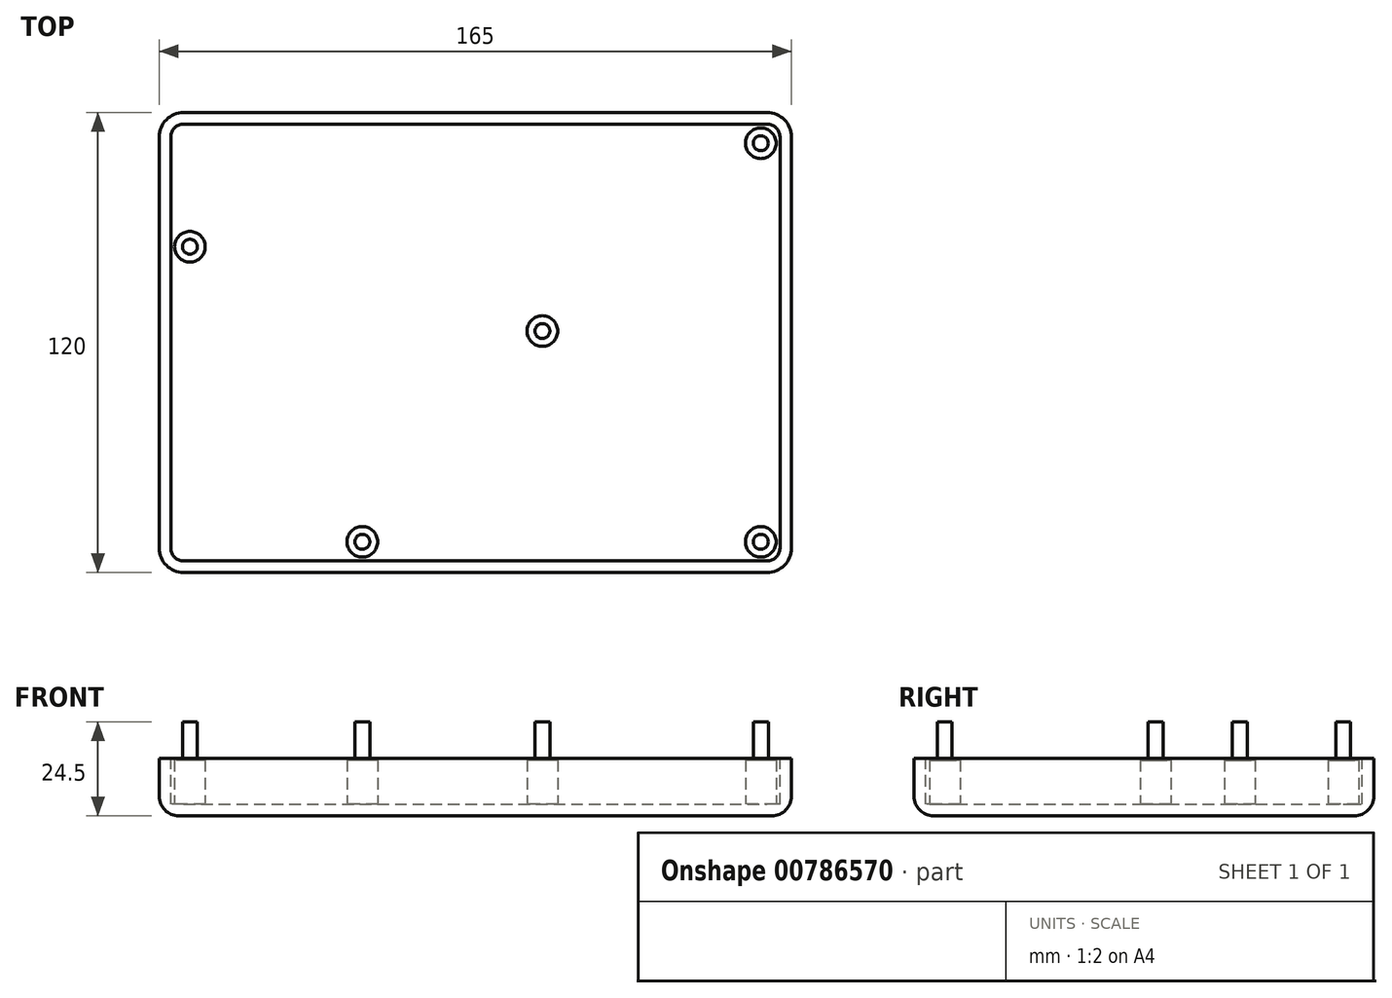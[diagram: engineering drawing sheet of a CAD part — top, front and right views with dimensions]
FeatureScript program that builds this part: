
annotation { "Feature Type Name" : "Feature", "Feature Type Description" : "" }
export const myFeature = defineFeature(function(context is Context, id is Id, definition is map)
    precondition{}
    {
        {
            var Q0;
            Q0=qCreatedBy(makeId("Top.planeOp"),FACE);
            var sketch = newSketch(context, id + "F0", { "sketchPlane" : qUnion([Q0])});
            skLineSegment(sketch, "E0.bottom", {"start": v(-76.98, -45.25) * mm, "end": v(75.32, -45.25) * mm});
            skLineSegment(sketch, "E0.top", {"start": v(-76.98, 74.75) * mm, "end": v(75.32, 74.75) * mm});
            skLineSegment(sketch, "E0.left", {"start": v(-83.33, -38.9) * mm, "end": v(-83.33, 68.4) * mm});
            skLineSegment(sketch, "E0.right", {"start": v(81.67, -38.9) * mm, "end": v(81.67, 68.4) * mm});
            skPoint(sketch, "E1.visualSharp", {"position": v(-83.33, 74.75) * mm});
            skArc(sketch, "E1.filletArc", {"start": v(-76.98, 74.75) * mm, "mid": v(-81.47, 72.89) * mm, "end": v(-83.33, 68.4) * mm});
            skPoint(sketch, "E2.visualSharp", {"position": v(81.67, 74.75) * mm});
            skArc(sketch, "E2.filletArc", {"start": v(81.67, 68.4) * mm, "mid": v(79.8, 72.89) * mm, "end": v(75.32, 74.75) * mm});
            skPoint(sketch, "E3.visualSharp", {"position": v(81.67, -45.25) * mm});
            skArc(sketch, "E3.filletArc", {"start": v(75.32, -45.25) * mm, "mid": v(79.8, -43.4) * mm, "end": v(81.67, -38.9) * mm});
            skPoint(sketch, "E4.visualSharp", {"position": v(-83.33, -45.25) * mm});
            skArc(sketch, "E4.filletArc", {"start": v(-83.33, -38.9) * mm, "mid": v(-81.47, -43.4) * mm, "end": v(-76.98, -45.25) * mm});
            skSolve(sketch);
        }
        {
            var Q0;
            Q0 = qSketchRegion(id + "F0", true);
            extrude(context, id + "F1", {"entities" : qUnion([Q0]), "depth" : 15 * mm, "offsetDistance" : 25.4 * mm});
        }
        {
            var Q0;
            Q0=makeQuery(id+"F1.opExtrude","CAP_FACE",FACE,{"disambiguationData":[OSD([sQuery(id+"F0.wireOp",EDGE,"E0.bottom"),sQuery(id+"F0.wireOp",EDGE,"E0.top"),sQuery(id+"F0.wireOp",EDGE,"E0.left"),sQuery(id+"F0.wireOp",EDGE,"E0.right")])],"isStart":false});
            shell(context, id + "F2", {"entities" : qUnion([Q0]), "thickness" : 3 * mm});
        }
        {
            var Q0;
            Q0=makeQuery(id+"F1.opExtrude","CAP_EDGE",EDGE,{"disambiguationData":[OSD([sQuery(id+"F0.wireOp",EDGE,"E1.filletArc")])],"isStart":true});
            fillet(context, id + "F3", {"entities" : qUnion([Q0]), "radius" : 5.08 * mm, "tangentPropagation" : true, "allowEdgeOverflow" : false});
        }
        {
            var Q0;
            Q0=makeQuery(id+"F2.opShell","OFFSET_FACE",FACE,{"disambiguationData":[OSD([sQuery(id+"F0.wireOp",EDGE,"E0.bottom"),sQuery(id+"F0.wireOp",EDGE,"E0.top"),sQuery(id+"F0.wireOp",EDGE,"E0.left"),sQuery(id+"F0.wireOp",EDGE,"E0.right"),sQuery(id+"F0.wireOp",EDGE,"E1.filletArc"),sQuery(id+"F0.wireOp",EDGE,"E2.filletArc"),sQuery(id+"F0.wireOp",EDGE,"E3.filletArc"),sQuery(id+"F0.wireOp",EDGE,"E4.filletArc")])]});
            var sketch = newSketch(context, id + "F4", { "sketchPlane" : qUnion([Q0])});
            skCircle(sketch, "E5", {"center": v(73.67, -37.25) * mm, "radius": 4 * mm});
            skCircle(sketch, "E6", {"center": v(73.67, 66.75) * mm, "radius": 4 * mm});
            skCircle(sketch, "E7", {"center": v(16.67, 17.75) * mm, "radius": 4 * mm});
            skCircle(sketch, "E8", {"center": v(-75.33, 39.75) * mm, "radius": 4 * mm});
            skCircle(sketch, "E9", {"center": v(-30.33, -37.25) * mm, "radius": 4 * mm});
            skSolve(sketch);
        }
        {
            var Q0;
            Q0 = qSketchRegion(id + "F4", true);
            extrude(context, id + "F5", {"entities" : qUnion([Q0]), "operationType" : NewBodyOperationType.ADD, "depth" : 11.5 * mm, "offsetDistance" : 25 * mm});
        }
        {
            var Q0;
            Q0=makeQuery(id+"F5.opExtrude","CAP_FACE",FACE,{"disambiguationData":[OSD([sQuery(id+"F4.wireOp",EDGE,"E5")])],"isStart":false});
            var sketch = newSketch(context, id + "F6", { "sketchPlane" : qUnion([Q0])});
            skCircle(sketch, "E10", {"center": v(73.67, -37.25) * mm, "radius": 1.95 * mm});
            skCircle(sketch, "E11", {"center": v(16.67, 17.75) * mm, "radius": 1.95 * mm});
            skCircle(sketch, "E12", {"center": v(73.67, 66.75) * mm, "radius": 1.95 * mm});
            skCircle(sketch, "E13", {"center": v(-30.33, -37.25) * mm, "radius": 1.95 * mm});
            skCircle(sketch, "E14", {"center": v(-75.33, 39.75) * mm, "radius": 1.95 * mm});
            skSolve(sketch);
        }
        {
            var Q0;
            Q0 = qSketchRegion(id + "F6", true);
            extrude(context, id + "F7", {"entities" : qUnion([Q0]), "operationType" : NewBodyOperationType.ADD, "depth" : 10 * mm, "offsetDistance" : 25 * mm});
        }
    });
